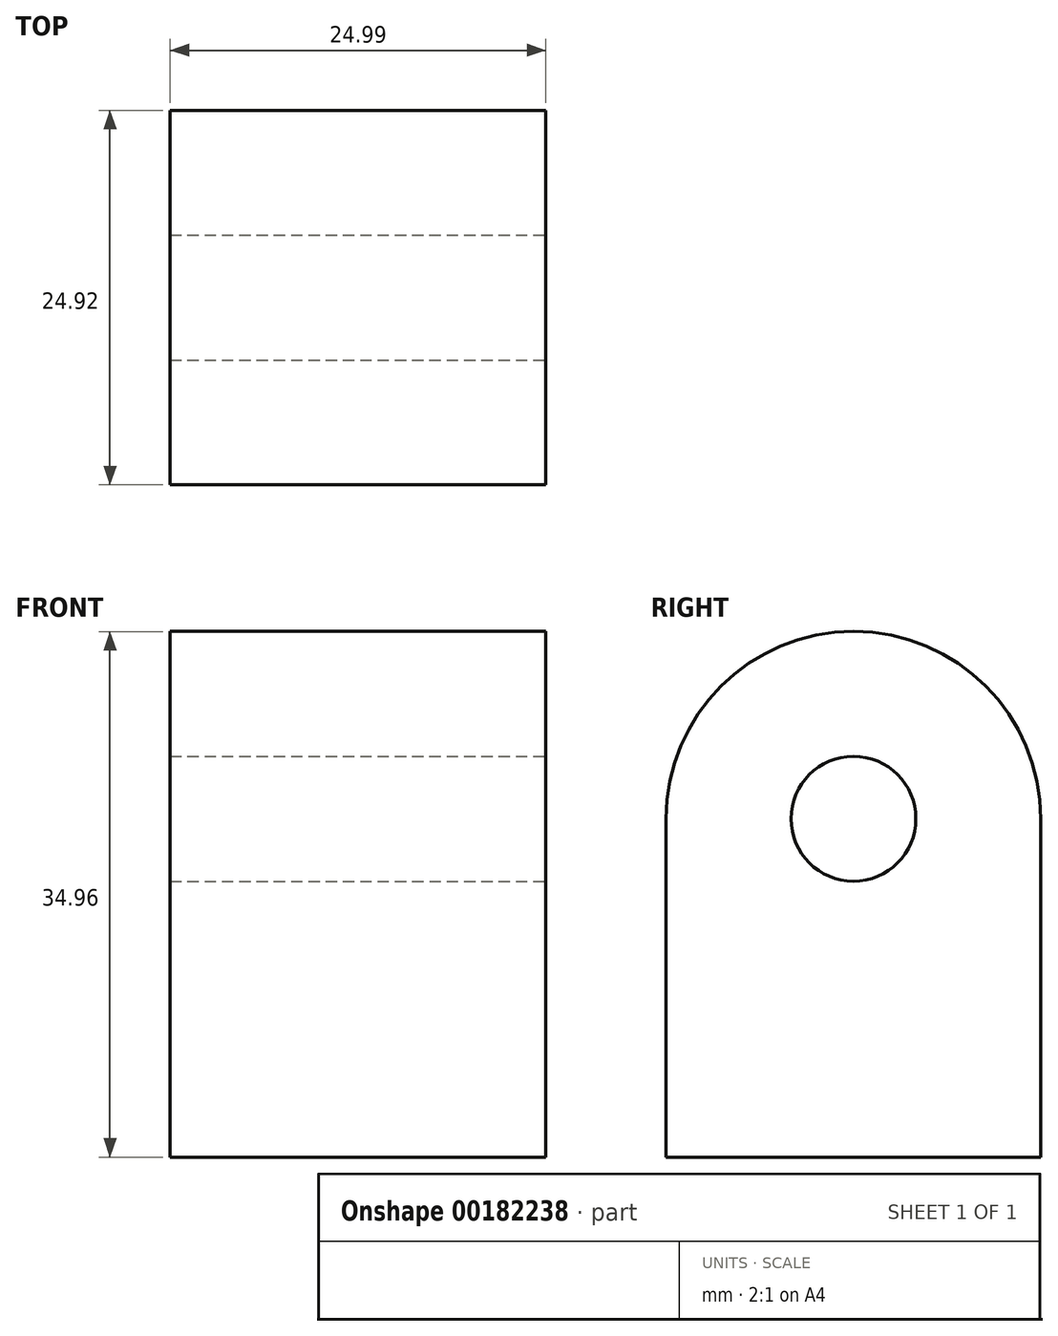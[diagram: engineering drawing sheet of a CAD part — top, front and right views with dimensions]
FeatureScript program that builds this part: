
annotation { "Feature Type Name" : "Feature", "Feature Type Description" : "" }
export const myFeature = defineFeature(function(context is Context, id is Id, definition is map)
    precondition{}
    {
        {
            var Q0;
            Q0=qCreatedBy(makeId("Right.planeOp"),FACE);
            var sketch = newSketch(context, id + "F0", { "sketchPlane" : qUnion([Q0])});
            skLineSegment(sketch, "E0.bottom", {"start": v(0, 0) * mm, "end": v(24.92, 0) * mm});
            skLineSegment(sketch, "E0.top", {"start": v(0, 22.5) * mm, "end": v(24.92, 22.5) * mm});
            skLineSegment(sketch, "E0.left", {"start": v(0, 0) * mm, "end": v(0, 22.5) * mm});
            skLineSegment(sketch, "E0.right", {"start": v(24.92, 0) * mm, "end": v(24.92, 22.5) * mm});
            skArc(sketch, "E1", {"start": v(24.92, 22.5) * mm, "mid": v(12.46, 34.96) * mm, "end": v(0, 22.5) * mm});
            skSolve(sketch);
        }
        {
            var Q0;
            Q0=qSketchRegion(id+"F0",true);
            extrude(context, id + "F1", {"entities" : qUnion([Q0]), "oppositeDirection" : true, "depth" : 25 * mm});
        }
        {
            var Q0;
            Q0=makeQuery(id+"F1.opExtrude","CAP_FACE",FACE,{"disambiguationData":[OSD([sQuery(id+"F0.wireOp",EDGE,"E0.bottom"),sQuery(id+"F0.wireOp",EDGE,"E0.left"),sQuery(id+"F0.wireOp",EDGE,"E0.right"),sQuery(id+"F0.wireOp",EDGE,"E1")])],"isStart":true});
            var sketch = newSketch(context, id + "F2", { "sketchPlane" : qUnion([Q0])});
            skCircle(sketch, "E2", {"center": v(12.46, 22.5) * mm, "radius": 4.15 * mm});
            skSolve(sketch);
        }
        {
            var Q0;
            Q0=qSketchRegion(id+"F2",true);
            extrude(context, id + "F3", {"entities" : qUnion([Q0]), "operationType" : NewBodyOperationType.REMOVE, "endBound" : BoundingType.THROUGH_ALL, "oppositeDirection" : true, "depth" : 25.4 * mm});
        }
    });
